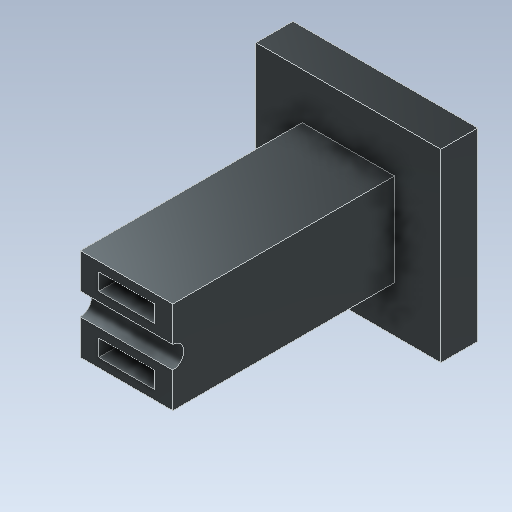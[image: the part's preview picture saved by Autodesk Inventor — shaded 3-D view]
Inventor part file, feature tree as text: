
AUTODESK INVENTOR PART (.ipt)
format: ipt  version: 2021 (Build 250183000, 183)  size: 155,136 bytes
history: native  units: in
note: dims shown in document units (in); Inventor stores cm internally (conversion verified against a paired STEP export)
features: extrude x4, sketch x4
ambient origin geometry x8: Origin, YZ Plane, XZ Plane, XY Plane, X Axis, Y Axis, Z Axis, Center Point
bodies: Solid1 (feature_tree)
feature tree (8):
  extrude  "Extrusion1"  Depth=3.937in
  extrude  "Extrusion2"  Depth=0.9843in
  extrude  "Extrusion3"  Depth=0.9843in
  extrude  "Extrusion4"  Depth=4.7244in TaperAngle=0.0deg
  sketch  "Sketch1"  dims[d0=3.937in d1=3.937in]
  sketch  "Sketch2"  dims[d2=0.7874in d3=0.0in d4=0.9843in]
  sketch  "Sketch3"  dims[d5=0.9843in d6=0.9843in]
  sketch  "Sketch4"  dims[d7=0.9843in d8=4.7244in d9=0.0in d10=0.4724in d11=1.9685in d12=0.0in d13=0.3937in d14=0.3937in d15=0.1969in d16=0.1969in d17=0.1969in d18=0.1969in d19=0.7874in d20=0.0in]
